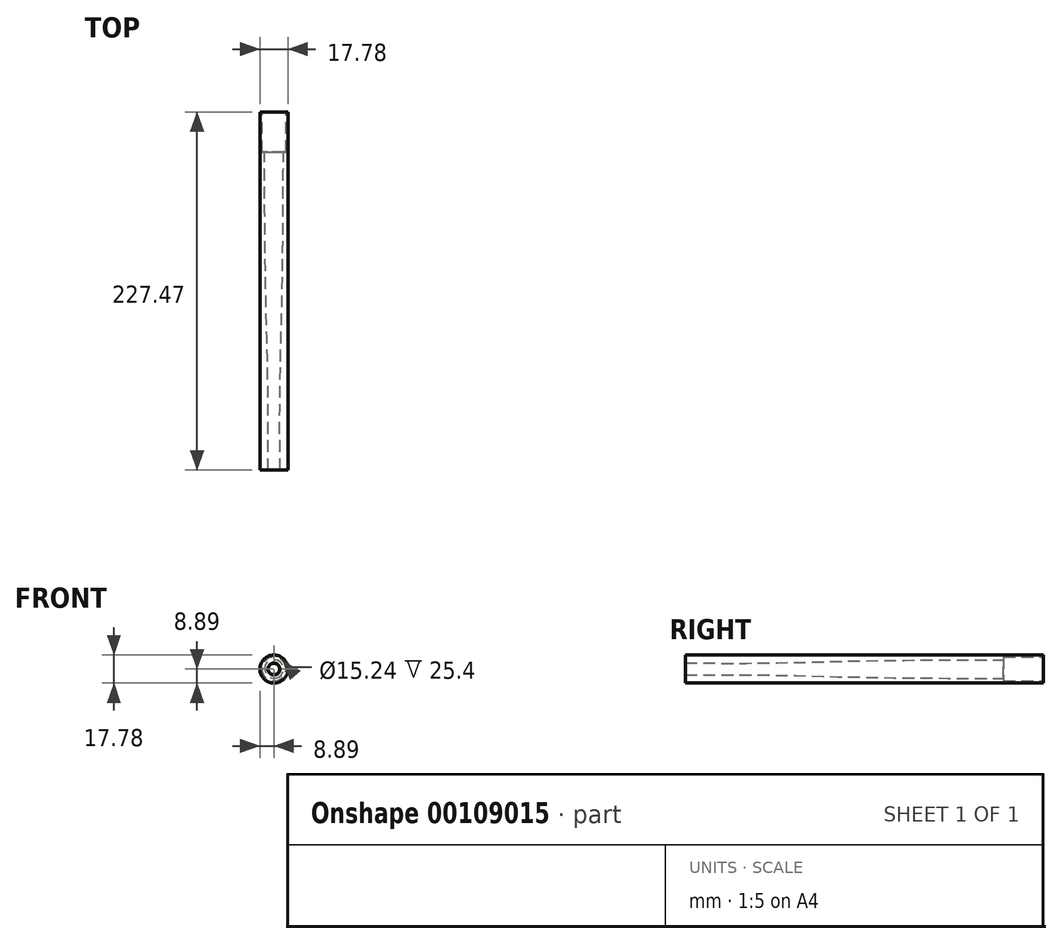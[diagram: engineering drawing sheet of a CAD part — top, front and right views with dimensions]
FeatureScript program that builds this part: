
annotation { "Feature Type Name" : "Feature", "Feature Type Description" : "" }
export const myFeature = defineFeature(function(context is Context, id is Id, definition is map)
    precondition{}
    {
        {
            var Q0;
            Q0=qCreatedBy(makeId("Front.planeOp"),FACE);
            var sketch = newSketch(context, id + "F0", { "sketchPlane" : qUnion([Q0])});
            skCircle(sketch, "E0", {"center": v(0, 0) * mm, "radius": 8.9 * mm});
            skSolve(sketch);
        }
        {
            var Q0;
            Q0=qCreatedBy(makeId("Top.planeOp"),FACE);
            var sketch = newSketch(context, id + "F1", { "sketchPlane" : qUnion([Q0])});
            skLineSegment(sketch, "E1", {"start": v(0, 0) * mm, "end": v(0, 49.31) * mm});
            skLineSegment(sketch, "E2", {"start": v(0, 49.31) * mm, "end": v(0, 106.6) * mm});
            skLineSegment(sketch, "E3", {"start": v(0, 106.6) * mm, "end": v(0, 167.03) * mm});
            skLineSegment(sketch, "E4", {"start": v(0, 167.03) * mm, "end": v(0, 227.47) * mm});
            skLineSegment(sketch, "E5", {"start": v(0, 0) * mm, "end": v(-18.36, 0) * mm});
            skLineSegment(sketch, "E6", {"start": v(-18.36, 0) * mm, "end": v(-18.36, 227.47) * mm});
            skSolve(sketch);
        }
        {
            var Q0;
            Q0=sQuery(id+"F1.wireOp",EDGE,"E1");
            var Q1;
            Q1=sQuery(id+"F1.wireOp",VERTEX,"E2.start");
            cPlane(context, id + "F2", {"entities" : qUnion([Q0, Q1]), "cplaneType" : CPlaneType.LINE_POINT, "offset" : 25.4 * mm, "width" : 152.4 * mm, "height" : 152.4 * mm});
        }
        {
            var Q0;
            Q0=sQuery(id+"F1.wireOp",EDGE,"E2");
            var Q1;
            Q1=sQuery(id+"F1.wireOp",VERTEX,"E3.start");
            cPlane(context, id + "F3", {"entities" : qUnion([Q0, Q1]), "cplaneType" : CPlaneType.LINE_POINT, "offset" : 25.4 * mm, "width" : 152.4 * mm, "height" : 152.4 * mm});
        }
        {
            var Q0;
            Q0=sQuery(id+"F1.wireOp",EDGE,"E3");
            var Q1;
            Q1=sQuery(id+"F1.wireOp",VERTEX,"E4.start");
            cPlane(context, id + "F4", {"entities" : qUnion([Q0, Q1]), "cplaneType" : CPlaneType.LINE_POINT, "offset" : 25.4 * mm, "width" : 152.4 * mm, "height" : 152.4 * mm});
        }
        {
            var Q0;
            Q0=sQuery(id+"F1.wireOp",EDGE,"E4");
            var Q1;
            Q1=sQuery(id+"F1.wireOp",VERTEX,"E4.end");
            cPlane(context, id + "F5", {"entities" : qUnion([Q0, Q1]), "cplaneType" : CPlaneType.LINE_POINT, "offset" : 25.4 * mm, "width" : 152.4 * mm, "height" : 152.4 * mm});
        }
        {
            var Q0;
            Q0=qCreatedBy(id+"F2.planeOp",FACE);
            var sketch = newSketch(context, id + "F6", { "sketchPlane" : qUnion([Q0])});
            skCircle(sketch, "E7", {"center": v(0, 0) * mm, "radius": 8.9 * mm});
            skSolve(sketch);
        }
        {
            var Q0;
            Q0=qCreatedBy(id+"F3.planeOp",FACE);
            var sketch = newSketch(context, id + "F7", { "sketchPlane" : qUnion([Q0])});
            skCircle(sketch, "E8", {"center": v(0, 0) * mm, "radius": 8.9 * mm});
            skSolve(sketch);
        }
        {
            var Q0;
            Q0=qCreatedBy(id+"F4.planeOp",FACE);
            var sketch = newSketch(context, id + "F8", { "sketchPlane" : qUnion([Q0])});
            skCircle(sketch, "E9", {"center": v(0, 0) * mm, "radius": 8.9 * mm});
            skSolve(sketch);
        }
        {
            var Q0;
            Q0=qCreatedBy(id+"F5.planeOp",FACE);
            var sketch = newSketch(context, id + "F9", { "sketchPlane" : qUnion([Q0])});
            skCircle(sketch, "E10", {"center": v(0, 0) * mm, "radius": 8.9 * mm});
            skSolve(sketch);
        }
        {
            var Q0;
            Q0=makeQuery(id+"F0.imprint","IMPRINT",FACE,{"disambiguationData":[TD([[makeQuery(id+"F0.imprint","IMPRINT",EDGE,{"derivedFrom":sQuery(id+"F0.wireOp",EDGE,"E0")}),1.0]])]});
            var Q1;
            Q1=makeQuery(id+"F6.imprint","IMPRINT",FACE,{"disambiguationData":[TD([[makeQuery(id+"F6.imprint","IMPRINT",EDGE,{"derivedFrom":sQuery(id+"F6.wireOp",EDGE,"E7")}),1.0]])]});
            var Q2;
            Q2=makeQuery(id+"F7.imprint","IMPRINT",FACE,{"disambiguationData":[TD([[makeQuery(id+"F7.imprint","IMPRINT",EDGE,{"derivedFrom":sQuery(id+"F7.wireOp",EDGE,"E8")}),1.0]])]});
            var Q3;
            Q3=makeQuery(id+"F8.imprint","IMPRINT",FACE,{"disambiguationData":[TD([[makeQuery(id+"F8.imprint","IMPRINT",EDGE,{"derivedFrom":sQuery(id+"F8.wireOp",EDGE,"E9")}),1.0]])]});
            var Q4;
            Q4=makeQuery(id+"F9.imprint","IMPRINT",FACE,{"disambiguationData":[TD([[makeQuery(id+"F9.imprint","IMPRINT",EDGE,{"derivedFrom":sQuery(id+"F9.wireOp",EDGE,"E10")}),1.0]])]});
            loft(context, id + "F10", {"sheetProfilesArray" : [{ "sheetProfileEntities" : qUnion([Q0]) }, { "sheetProfileEntities" : qUnion([Q1]) }, { "sheetProfileEntities" : qUnion([Q2]) }, { "sheetProfileEntities" : qUnion([Q3]) }, { "sheetProfileEntities" : qUnion([Q4]) }]});
        }
        {
            var Q0;
            Q0=qCreatedBy(makeId("Front.planeOp"),FACE);
            var sketch = newSketch(context, id + "F11", { "sketchPlane" : qUnion([Q0])});
            skCircle(sketch, "E11", {"center": v(0, 0) * mm, "radius": 3.81 * mm});
            skSolve(sketch);
        }
        {
            var Q0;
            Q0=qCreatedBy(id+"F2.planeOp",FACE);
            var sketch = newSketch(context, id + "F12", { "sketchPlane" : qUnion([Q0])});
            skCircle(sketch, "E12", {"center": v(0, 0) * mm, "radius": 3.81 * mm});
            skSolve(sketch);
        }
        {
            var Q0;
            Q0=qCreatedBy(id+"F3.planeOp",FACE);
            var sketch = newSketch(context, id + "F13", { "sketchPlane" : qUnion([Q0])});
            skCircle(sketch, "E13", {"center": v(0, 0) * mm, "radius": 5.08 * mm});
            skSolve(sketch);
        }
        {
            var Q0;
            Q0=qCreatedBy(id+"F4.planeOp",FACE);
            var sketch = newSketch(context, id + "F14", { "sketchPlane" : qUnion([Q0])});
            skCircle(sketch, "E14", {"center": v(0, 0) * mm, "radius": 5.84 * mm});
            skSolve(sketch);
        }
        {
            var Q0;
            Q0=qCreatedBy(id+"F5.planeOp",FACE);
            var sketch = newSketch(context, id + "F15", { "sketchPlane" : qUnion([Q0])});
            skCircle(sketch, "E15", {"center": v(0, 0) * mm, "radius": 5.97 * mm});
            skSolve(sketch);
        }
        {
            var Q0;
            Q0=makeQuery(id+"F11.imprint","IMPRINT",FACE,{"disambiguationData":[TD([[makeQuery(id+"F11.imprint","IMPRINT",EDGE,{"derivedFrom":sQuery(id+"F11.wireOp",EDGE,"E11")}),1.0]])]});
            var Q1;
            Q1=makeQuery(id+"F12.imprint","IMPRINT",FACE,{"disambiguationData":[TD([[makeQuery(id+"F12.imprint","IMPRINT",EDGE,{"derivedFrom":sQuery(id+"F12.wireOp",EDGE,"E12")}),1.0]])]});
            var Q2;
            Q2=makeQuery(id+"F13.imprint","IMPRINT",FACE,{"disambiguationData":[TD([[makeQuery(id+"F13.imprint","IMPRINT",EDGE,{"derivedFrom":sQuery(id+"F13.wireOp",EDGE,"E13")}),1.0]])]});
            var Q3;
            Q3=makeQuery(id+"F14.imprint","IMPRINT",FACE,{"disambiguationData":[TD([[makeQuery(id+"F14.imprint","IMPRINT",EDGE,{"derivedFrom":sQuery(id+"F14.wireOp",EDGE,"E14")}),1.0]])]});
            var Q4;
            Q4=makeQuery(id+"F15.imprint","IMPRINT",FACE,{"disambiguationData":[TD([[makeQuery(id+"F15.imprint","IMPRINT",EDGE,{"derivedFrom":sQuery(id+"F15.wireOp",EDGE,"E15")}),1.0]])]});
            loft(context, id + "F16", {"operationType" : NewBodyOperationType.REMOVE, "sheetProfilesArray" : [{ "sheetProfileEntities" : qUnion([Q0]) }, { "sheetProfileEntities" : qUnion([Q1]) }, { "sheetProfileEntities" : qUnion([Q2]) }, { "sheetProfileEntities" : qUnion([Q3]) }, { "sheetProfileEntities" : qUnion([Q4]) }]});
        }
        {
            var Q0;
            Q0=makeQuery(id+"F10.opLoft","CAP_FACE",FACE,{"disambiguationData":[OSD([makeQuery(id+"F9.imprint","IMPRINT",FACE,{"disambiguationData":[TD([[makeQuery(id+"F9.imprint","IMPRINT",EDGE,{"derivedFrom":sQuery(id+"F9.wireOp",EDGE,"E10")}),1.0]])]})])],"isStart":true});
            var sketch = newSketch(context, id + "F17", { "sketchPlane" : qUnion([Q0])});
            skCircle(sketch, "E16", {"center": v(0, 0) * mm, "radius": 7.62 * mm});
            skSolve(sketch);
        }
        {
            var Q0;
            Q0=makeQuery(id+"F17.imprint","IMPRINT",FACE,{"disambiguationData":[TD([[makeQuery(id+"F17.imprint","IMPRINT",EDGE,{"derivedFrom":sQuery(id+"F17.wireOp",EDGE,"E16")}),1.0]])]});
            extrude(context, id + "F18", {"entities" : qUnion([Q0]), "operationType" : NewBodyOperationType.ADD, "depth" : 12.7 * mm});
        }
        {
            var Q0;
            Q0=makeQuery(id+"F18.opExtrude","CAP_FACE",FACE,{"disambiguationData":[OSD([sQuery(id+"F11.wireOp",EDGE,"E11"),sQuery(id+"F15.wireOp",EDGE,"E15"),sQuery(id+"F17.wireOp",EDGE,"E16")])],"isStart":false});
            extrude(context, id + "F19", {"entities" : qUnion([Q0]), "operationType" : NewBodyOperationType.REMOVE, "oppositeDirection" : true, "depth" : 38.1 * mm});
        }
        {
            var Q0;
            Q0=makeQuery(id+"F15.imprint","IMPRINT",FACE,{"disambiguationData":[TD([[makeQuery(id+"F15.imprint","IMPRINT",EDGE,{"derivedFrom":sQuery(id+"F15.wireOp",EDGE,"E15")}),1.0]])]});
            extrude(context, id + "F20", {"entities" : qUnion([Q0]), "operationType" : NewBodyOperationType.REMOVE, "oppositeDirection" : true, "depth" : 25.4 * mm});
        }
    });
